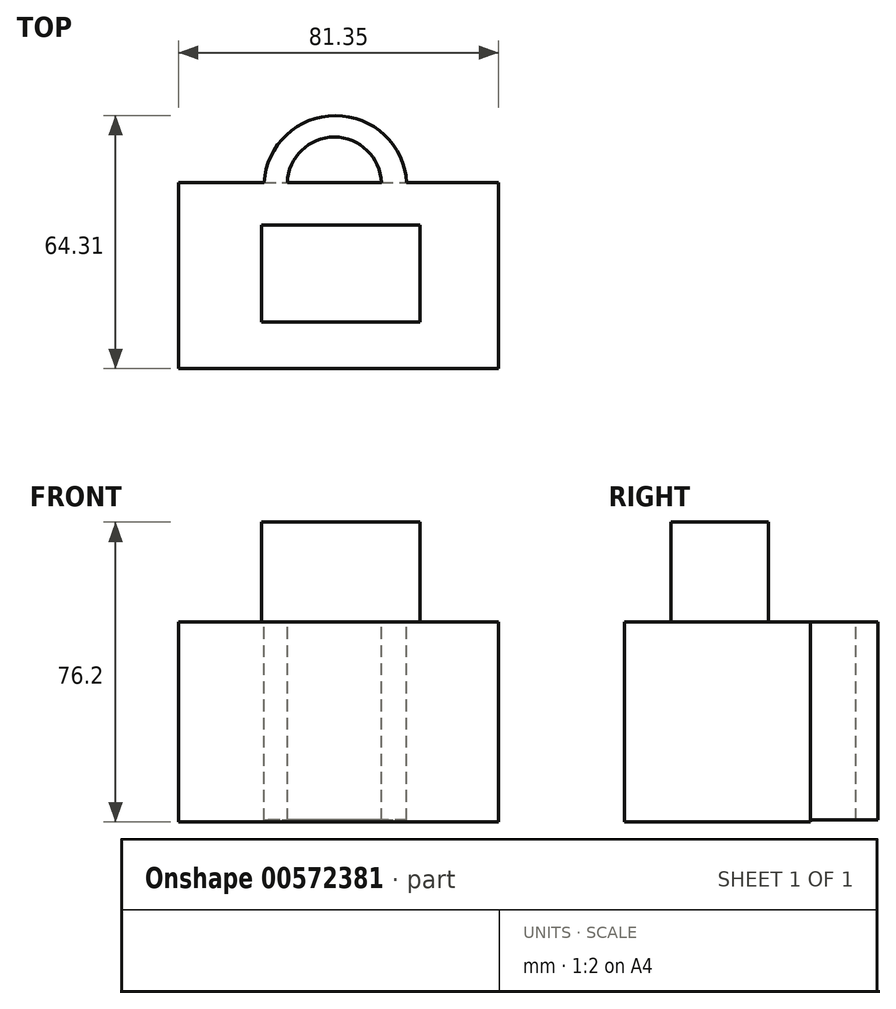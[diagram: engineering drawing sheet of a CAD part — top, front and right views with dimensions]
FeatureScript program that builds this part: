
annotation { "Feature Type Name" : "Feature", "Feature Type Description" : "" }
export const myFeature = defineFeature(function(context is Context, id is Id, definition is map)
    precondition{}
    {
        {
            var Q0;
            Q0=qCreatedBy(makeId("Top.planeOp"),FACE);
            var sketch = newSketch(context, id + "F0", { "sketchPlane" : qUnion([Q0])});
            skLineSegment(sketch, "E0.bottom", {"start": v(-39.2, 28.2) * mm, "end": v(42.15, 28.2) * mm});
            skLineSegment(sketch, "E0.top", {"start": v(-39.2, -19.06) * mm, "end": v(42.15, -19.06) * mm});
            skLineSegment(sketch, "E0.left", {"start": v(-39.2, 28.2) * mm, "end": v(-39.2, -19.06) * mm});
            skLineSegment(sketch, "E0.right", {"start": v(42.15, 28.2) * mm, "end": v(42.15, -19.06) * mm});
            skSolve(sketch);
        }
        {
            var Q0;
            Q0 = qSketchRegion(id + "F0", true);
            extrude(context, id + "F1", {"entities" : qUnion([Q0]), "depth" : 25.4 * mm, "offsetDistance" : 25.4 * mm});
        }
        {
            var Q0;
            Q0=makeQuery(id+"F1.opExtrude","CAP_FACE",FACE,{"disambiguationData":[OSD([sQuery(id+"F0.wireOp",EDGE,"E0.bottom"),sQuery(id+"F0.wireOp",EDGE,"E0.top"),sQuery(id+"F0.wireOp",EDGE,"E0.left"),sQuery(id+"F0.wireOp",EDGE,"E0.right")])],"isStart":false});
            var sketch = newSketch(context, id + "F2", { "sketchPlane" : qUnion([Q0])});
            skArc(sketch, "E1", {"start": v(12.35, 28.2) * mm, "mid": v(0.4, 39.76) * mm, "end": v(-11.55, 28.2) * mm});
            skArc(sketch, "E2", {"start": v(18.8, 28.2) * mm, "mid": v(0.67, 45.25) * mm, "end": v(-17.45, 28.2) * mm});
            skSolve(sketch);
        }
        {
            var Q0;
            {var subQ0=sQuery(id+"F2.wireOp",EDGE,"E1");Q0=makeQuery(id+"F2.imprint","IMPRINT",FACE,{"disambiguationData":[TD([[makeQuery(id+"F2.imprint","IMPRINT",EDGE,{"derivedFrom":subQ0}),-1.0]])]});}
            extrude(context, id + "F3", {"entities" : qUnion([Q0]), "operationType" : NewBodyOperationType.ADD, "oppositeDirection" : true, "depth" : 24.9 * mm, "offsetDistance" : 25.4 * mm});
        }
        {
            var Q0;
            Q0=makeQuery(id+"F0.imprint","IMPRINT",FACE,{"disambiguationData":[TD([[makeQuery(id+"F0.imprint","IMPRINT",EDGE,{"derivedFrom":sQuery(id+"F0.wireOp",EDGE,"E0.bottom")}),-1.0]])]});
            var Q1;
            {var subQ0=sQuery(id+"F0.wireOp",EDGE,"E0.bottom");Q1=makeQuery(id+"F3.boolean.opBoolean","MERGE",FACE,{"derivedFrom":[makeQuery(id+"F1.opExtrude","CAP_FACE",FACE,{"disambiguationData":[OSD([subQ0,sQuery(id+"F0.wireOp",EDGE,"E0.top"),sQuery(id+"F0.wireOp",EDGE,"E0.left"),sQuery(id+"F0.wireOp",EDGE,"E0.right")])],"isStart":false}),makeQuery(id+"F3.opExtrude","CAP_FACE",FACE,{"disambiguationData":[OSD([subQ0,sQuery(id+"F2.wireOp",EDGE,"E1"),sQuery(id+"F2.wireOp",EDGE,"E2")])],"isStart":true})]});}
            var Q2;
            Q2=makeQuery(id+"F1.opExtrude","CAP_FACE",FACE,{"disambiguationData":[OSD([sQuery(id+"F0.wireOp",EDGE,"E0.bottom"),sQuery(id+"F0.wireOp",EDGE,"E0.top"),sQuery(id+"F0.wireOp",EDGE,"E0.left"),sQuery(id+"F0.wireOp",EDGE,"E0.right")])],"isStart":true});
            extrude(context, id + "F4", {"entities" : qUnion([Q0, Q1, Q2]), "operationType" : NewBodyOperationType.ADD, "depth" : 25.4 * mm, "offsetDistance" : 25.4 * mm});
        }
        {
            var Q0;
            Q0=makeQuery(id+"F4.opExtrude","CAP_FACE",FACE,{"disambiguationData":[OSD([sQuery(id+"F0.wireOp",EDGE,"E0.bottom"),sQuery(id+"F0.wireOp",EDGE,"E0.top"),sQuery(id+"F0.wireOp",EDGE,"E0.left"),sQuery(id+"F0.wireOp",EDGE,"E0.right"),sQuery(id+"F2.wireOp",EDGE,"E1"),sQuery(id+"F2.wireOp",EDGE,"E2")])],"isStart":false});
            var sketch = newSketch(context, id + "F5", { "sketchPlane" : qUnion([Q0])});
            skLineSegment(sketch, "E3.bottom", {"start": v(-18.12, 17.45) * mm, "end": v(22.15, 17.45) * mm});
            skLineSegment(sketch, "E3.top", {"start": v(-18.12, -7.25) * mm, "end": v(22.15, -7.25) * mm});
            skLineSegment(sketch, "E3.left", {"start": v(-18.12, 17.45) * mm, "end": v(-18.12, -7.25) * mm});
            skLineSegment(sketch, "E3.right", {"start": v(22.15, 17.45) * mm, "end": v(22.15, -7.25) * mm});
            skSolve(sketch);
        }
        {
            var Q0;
            Q0 = qSketchRegion(id + "F5", true);
            extrude(context, id + "F6", {"entities" : qUnion([Q0]), "operationType" : NewBodyOperationType.ADD, "depth" : 25.4 * mm, "offsetDistance" : 25.4 * mm});
        }
    });
